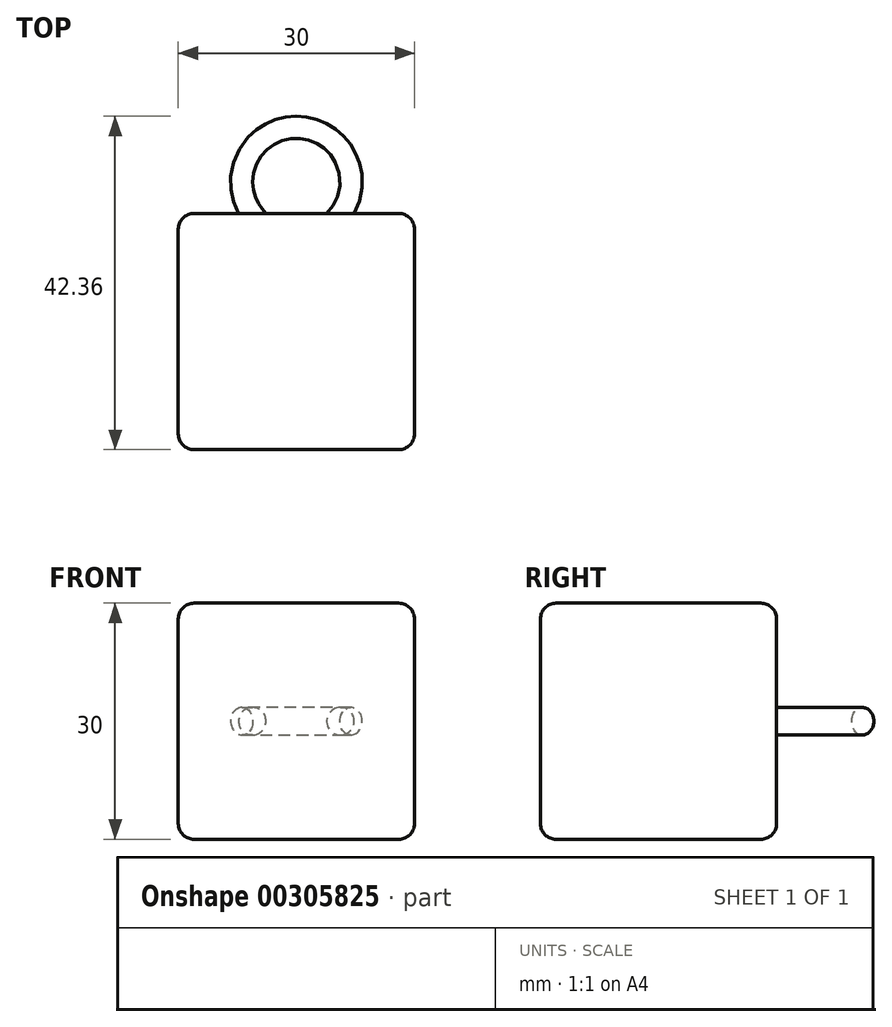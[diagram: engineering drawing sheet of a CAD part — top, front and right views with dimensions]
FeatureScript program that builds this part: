
annotation { "Feature Type Name" : "Feature", "Feature Type Description" : "" }
export const myFeature = defineFeature(function(context is Context, id is Id, definition is map)
    precondition{}
    {
        {
            var Q0;
            Q0=qCreatedBy(makeId("Top.planeOp"),FACE);
            var sketch = newSketch(context, id + "F0", { "sketchPlane" : qUnion([Q0])});
            skLineSegment(sketch, "E0.bottom", {"start": v(15, 15) * mm, "end": v(-15, 15) * mm});
            skLineSegment(sketch, "E0.top", {"start": v(15, -15) * mm, "end": v(-15, -15) * mm});
            skLineSegment(sketch, "E0.left", {"start": v(15, 15) * mm, "end": v(15, -15) * mm});
            skLineSegment(sketch, "E0.right", {"start": v(-15, 15) * mm, "end": v(-15, -15) * mm});
            skPoint(sketch, "E0.middle", {"position": v(0, 0) * mm});
            skSolve(sketch);
        }
        {
            var Q0;
            Q0=makeQuery(id+"F0.imprint","IMPRINT",FACE,{"disambiguationData":[TD([[makeQuery(id+"F0.imprint","IMPRINT",EDGE,{"derivedFrom":sQuery(id+"F0.wireOp",EDGE,"E0.bottom")}),1.0]])]});
            extrude(context, id + "F1", {"entities" : qUnion([Q0]), "endBound" : BoundingType.SYMMETRIC, "depth" : 30 * mm});
        }
        {
            var Q0;
            Q0=makeQuery(id+"F1.opExtrude","CAP_FACE",FACE,{"disambiguationData":[OSD([sQuery(id+"F0.wireOp",EDGE,"E0.bottom"),sQuery(id+"F0.wireOp",EDGE,"E0.top"),sQuery(id+"F0.wireOp",EDGE,"E0.left"),sQuery(id+"F0.wireOp",EDGE,"E0.right")])],"isStart":false});
            var Q1;
            Q1=makeQuery(id+"F1.opExtrude","SWEPT_FACE",FACE,{"disambiguationData":[OSD([sQuery(id+"F0.wireOp",EDGE,"E0.top")])]});
            var Q2;
            Q2=makeQuery(id+"F1.opExtrude","SWEPT_FACE",FACE,{"disambiguationData":[OSD([sQuery(id+"F0.wireOp",EDGE,"E0.left")])]});
            var Q3;
            Q3=makeQuery(id+"F1.opExtrude","SWEPT_FACE",FACE,{"disambiguationData":[OSD([sQuery(id+"F0.wireOp",EDGE,"E0.bottom")])]});
            var Q4;
            Q4=makeQuery(id+"F1.opExtrude","SWEPT_FACE",FACE,{"disambiguationData":[OSD([sQuery(id+"F0.wireOp",EDGE,"E0.right")])]});
            var Q5;
            Q5=makeQuery(id+"F1.opExtrude","CAP_FACE",FACE,{"disambiguationData":[OSD([sQuery(id+"F0.wireOp",EDGE,"E0.bottom"),sQuery(id+"F0.wireOp",EDGE,"E0.top"),sQuery(id+"F0.wireOp",EDGE,"E0.left"),sQuery(id+"F0.wireOp",EDGE,"E0.right")])],"isStart":true});
            fillet(context, id + "F2", {"entities" : qUnion([Q0, Q1, Q2, Q3, Q4, Q5]), "radius" : 2 * mm, "tangentPropagation" : true, "allowEdgeOverflow" : false});
        }
        {
            var Q0;
            Q0=qCreatedBy(makeId("Top.planeOp"),FACE);
            var sketch = newSketch(context, id + "F3", { "sketchPlane" : qUnion([Q0])});
            skLineSegment(sketch, "E1.0", {"start": v(13, 13) * mm, "end": v(-13, 13) * mm});
            skCircle(sketch, "E2", {"center": v(0, 19) * mm, "radius": 5 * mm});
            skPoint(sketch, "E2.centerSnap0", {"position": v(0, 13) * mm});
            skCircle(sketch, "E3.0", {"center": v(0, 19) * mm, "radius": 7 * mm});
            skSolve(sketch);
        }
        {
            var Q0;
            Q0=makeQuery(id+"F1.opExtrude","SWEPT_FACE",FACE,{"disambiguationData":[OSD([sQuery(id+"F0.wireOp",EDGE,"E0.bottom")])]});
            var sketch = newSketch(context, id + "F4", { "sketchPlane" : qUnion([Q0])});
            skCircle(sketch, "E4", {"center": v(5.6, 0) * mm, "radius": 1.75 * mm});
            skSolve(sketch);
        }
        {
            var Q0;
            Q0=makeQuery(id+"F4.imprint","IMPRINT",FACE,{"disambiguationData":[TD([[makeQuery(id+"F4.imprint","IMPRINT",EDGE,{"derivedFrom":sQuery(id+"F4.wireOp",EDGE,"E4")}),1.0]])]});
            var Q1;
            Q1=sQuery(id+"F3.wireOp",EDGE,"E3.0");
            sweep(context, id + "F5", {"operationType" : NewBodyOperationType.ADD, "profiles" : qUnion([Q0]), "path" : qUnion([Q1])});
        }
    });
